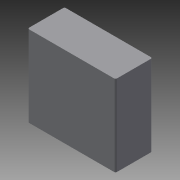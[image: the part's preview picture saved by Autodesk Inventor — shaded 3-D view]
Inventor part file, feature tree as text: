
AUTODESK INVENTOR PART (.ipt)
format: ipt  version: 2014 SP1 (Build 180222100, 222)  size: 76,288 bytes
history: native  units: in
note: dims shown in document units (in); Inventor stores cm internally (conversion verified against a paired STEP export)
features: extrude x1, fillet x1, sketch x1
ambient origin geometry x8: Origin, YZ Plane, XZ Plane, XY Plane, X Axis, Y Axis, Z Axis, Center Point
bodies: Solid1 (feature_tree)
feature tree (3):
  extrude  "Extrusion1"  Depth=6.57in
  fillet  "Fillet1"  Radius=2.99in
  sketch  "Sketch1"  dims[d0=7.13in d1=6.57in d2=2.99in d3=0.0in d4=0.125in]
